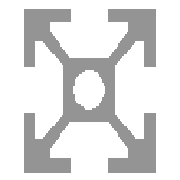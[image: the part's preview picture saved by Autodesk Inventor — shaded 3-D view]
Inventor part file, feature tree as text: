
AUTODESK INVENTOR PART (.ipt)
format: ipt  version: 2023 (Build 270158000, 158)  size: 233,984 bytes
history: native  units: in
note: dims shown in document units (in); Inventor stores cm internally (conversion verified against a paired STEP export)
features: other x37, extrude x1, fillet x1, sketch x1
ambient origin geometry x8: Origin, YZ Plane, XZ Plane, XY Plane, X Axis, Y Axis, Z Axis, Center Point
bodies: Body1 (feature_tree)
feature tree (40):
  other  "Table"
  other  "20x20 Channel-10"
  other  "20x20 Channel-20"
  other  "20x20 Channel-30"
  other  "20x20 Channel-40"
  other  "20x20 Channel-50"
  other  "20x20 Channel-100"
  other  "20x20 Channel-150"
  other  "20x20 Channel-200"
  other  "20x20 Channel-250"
  other  "20x20 Channel-300"
  other  "20x20 Channel-350"
  other  "20x20 Channel-400"
  other  "20x20 Channel-450"
  other  "20x20 Channel-500"
  other  "20x20 Channel-550"
  other  "20x20 Channel-560"
  other  "20x20 Channel-570"
  other  "20x20 Channel-580"
  other  "20x20 Channel-590"
  other  "20x20 Channel-600"
  other  "20x20 Channel-610"
  other  "20x20 Channel-620"
  other  "20x20 Channel-630"
  other  "20x20 Channel-640"
  other  "20x20 Channel-650"
  other  "CH-1-01-20x20 Channel-427"
  other  "CH-1-01-20x20 Channel-428"
  other  "CH-1-01-20x20 Channel-372"
  other  "CH-1-01-20x20 Channel-437"
  other  "CH-1-01-20x20 Channel-604"
  other  "CH-1-01-20x20 Channel-528"
  other  "CH-1-01-20x20 Channel-900"
  other  "CH-1-01-20x20 Channel-540"
  other  "CH-1-01-20x20 Channel-860"
  other  "CH-1-01-20x20 Channel-270"
  other  "CH-1-01-20x20 Channel-37.5"
  extrude  "Extrusion3"  Depth=0.7874in
  fillet  "Fillet2"  Radius=0.1969in
  sketch  "Sketch2"  dims[d0=0.7874in d1=0.7874in d2=0.1969in d3=0.2402in d4=0.2402in d5=0.2441in d6=0.0551in d7=0.0276in d8=45.0deg d9=0.0551in d10=1.5748in d12=360.0deg d27=1.4764in d28=0.0in d29=0.0394in d30=0.0394in]
